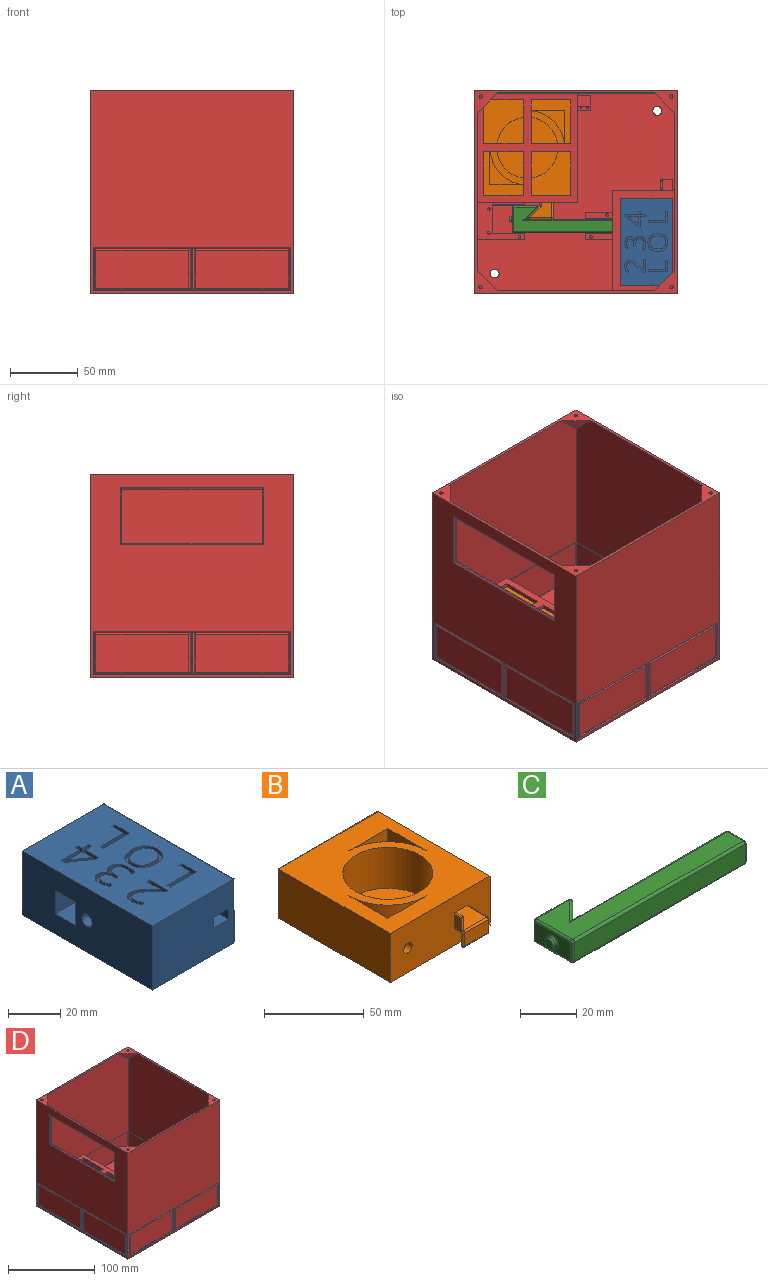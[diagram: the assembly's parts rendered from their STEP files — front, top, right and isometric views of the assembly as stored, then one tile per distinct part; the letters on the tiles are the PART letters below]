
ASSEMBLY  parts=4 mates=2
PART A: 132 faces, bbox 45.2x70.7x31.2 mm
  f0: plane 70.5x44mm, normal (0,0,1), area 2702.5mm2, adj f1,f7,f9,f11,f29,f30,f31,f32
  f1: plane 70.5x30mm, normal (-1,0,0), area 1970.2mm2, adj f0,f7,f9,f10,f18,f24,f25,f26
  f2: plane 8x5mm, normal (0,0,1), area 40mm2, adj f3,f5,f6,f7
  f3: plane 5x5mm, normal (1,0,0), area 25mm2, adj f2,f4,f6,f7
  f4: plane 8x5mm, normal (0,0,-1), area 40mm2, adj f3,f5,f6,f7
  f5: plane 5x5mm, normal (-1,0,0), area 25mm2, adj f2,f4,f6,f7
  f6: plane 8x5mm, normal (0,-1,0), area 40mm2, adj f2,f3,f4,f5
  f7: plane 44x30mm, normal (0,-1,0), area 1280mm2, adj f0,f1,f2,f3,f4,f5,f10,f12
  f8: plane 68.5x28mm, normal (1,0,0), area 1918mm2, adj f11,f12,f13,f14
  f9: plane 44x30mm, normal (0,1,0), area 1280mm2, adj f0,f1,f10,f13,f19,f20,f21,f22
  f10: plane 70.5x44mm, normal (0,0,-1), area 3065.1mm2, adj f1,f7,f9,f14,f15,f130
  f11: cylinder r=1mm len=70.5mm, axis (0,-1,0), area 109.6mm2, adj f0,f8,f12,f13
  f12: cylinder r=1mm len=30mm, axis (0,0,1), area 46mm2, adj f7,f8,f11,f14
  f13: cylinder r=1mm len=30mm, axis (0,0,-1), area 46mm2, adj f8,f9,f11,f14
  f14: cylinder r=1mm len=70.5mm, axis (0,1,0), area 109.6mm2, adj f8,f10,f12,f13
  f15: cylinder r=3.3mm len=17mm, axis (0,0,-1), area 248.2mm2, adj f10,f16,f130,f131
  f16: cone r=0mm half-angle=59deg, axis (0,0,-1), area 39.2mm2, adj f15,f130,f131
  f17: cone r=0mm half-angle=59deg, axis (-1,0,0), area 27.7mm2, adj f18
  f18: cylinder r=2.75mm len=10mm, axis (-1,0,0), area 172.8mm2, adj f1,f17
  f19: plane 5x5mm, normal (1,0,0), area 25mm2, adj f9,f20,f21,f23
  f20: plane 8x5mm, normal (0,0,-1), area 40mm2, adj f9,f19,f22,f23
  f21: plane 8x5mm, normal (0,0,1), area 40mm2, adj f9,f19,f22,f23
  f22: plane 5x5mm, normal (-1,0,0), area 25mm2, adj f9,f20,f21,f23
  f23: plane 8x5mm, normal (0,1,0), area 40mm2, adj f19,f20,f21,f22
  f24: plane 15x11mm, normal (0,0,-1), area 165mm2, adj f1,f25,f27,f28
  f25: plane 15x11mm, normal (0,-1,0), area 165mm2, adj f1,f24,f26,f28
  f26: plane 15x11mm, normal (0,0,1), area 165mm2, adj f1,f25,f27,f28
  f27: plane 15x11mm, normal (0,1,0), area 165mm2, adj f1,f24,f26,f28
  f28: plane 11x11mm, normal (-1,0,0), area 121mm2, adj f24,f25,f26,f27
  f29: plane 9.78x2mm, normal (-1,0,0), area 19.6mm2, adj f0,f30,f48,f49
  f30: plane 2x1.57mm, normal (0,-1,0), area 3.1mm2, adj f0,f29,f31,f49
  f31: plane 7.65x2mm, normal (1,0,0), area 15.3mm2, adj f0,f30,f32,f49
  f32: plane 2x0.08mm, normal (0,-1,0), area 0.2mm2, adj f0,f31,f33,f49
  f33: plane 3.26x3.18mm, normal (-0.71,-0.7,0), area 9.1mm2, adj f0,f32,f34,f49
  f34: extruded ~3.5x2.97mm, area 9.2mm2, adj f0,f33,f35,f49
  f35: extruded ~2.8x2mm, area 5.9mm2, adj f0,f34,f36,f49
  f36: extruded ~2.88x2mm, area 6.4mm2, adj f0,f35,f37,f49
  f37: extruded ~3.29x2mm, area 7.1mm2, adj f0,f36,f38,f49
  f38: extruded ~4.48x2mm, area 9.8mm2, adj f0,f37,f39,f49
  f39: plane 2x1.15mm, normal (-0.61,0.79,0), area 2.9mm2, adj f0,f38,f40,f49
  f40: extruded ~2x1.85mm, area 4.3mm2, adj f0,f39,f41,f49
  f41: extruded ~2x1.75mm, area 3.6mm2, adj f0,f40,f42,f49
  f42: extruded ~2.01x2mm, area 4.4mm2, adj f0,f41,f43,f49
  f43: extruded ~2x1.89mm, area 4.2mm2, adj f0,f42,f44,f49
  f44: extruded ~2x1.58mm, area 3.2mm2, adj f0,f43,f45,f49
  f45: extruded ~2x1.51mm, area 3.5mm2, adj f0,f44,f46,f49
  f46: extruded ~2.59x2.36mm, area 7mm2, adj f0,f45,f47,f49
  f47: plane 3.94x3.92mm, normal (0.71,0.71,0), area 11.1mm2, adj f0,f46,f48,f49
  f48: plane 2x1.46mm, normal (0,1,0), area 2.9mm2, adj f0,f29,f47,f49
  f49: plane 15.08x9.78mm, normal (0,0,1), area 48.7mm2, adj f29,f30,f31,f32,f33,f34,f35,f36
  f50: extruded ~4.39x2mm, area 9.3mm2, adj f51,f65,f66,f128
  f51: extruded ~4.35x2mm, area 9.2mm2, adj f50,f52,f66,f128
  f52: extruded ~3.6x2mm, area 8.1mm2, adj f51,f53,f66,f128
  f53: extruded ~3.56x2mm, area 8mm2, adj f52,f54,f66,f128
  f54: extruded ~4.36x2mm, area 9.2mm2, adj f53,f55,f66,f128
  f55: extruded ~4.4x2mm, area 9.3mm2, adj f54,f56,f66,f128
  f56: extruded ~3.58x2mm, area 8mm2, adj f55,f65,f66,f128
  f57: extruded ~5.38x2mm, area 11.6mm2, adj f0,f58,f64,f66
  f58: extruded ~5.38x2mm, area 11.6mm2, adj f0,f57,f59,f66
  f59: extruded ~4.8x2mm, area 10.7mm2, adj f0,f58,f60,f66
  f60: extruded ~4.87x2mm, area 10.8mm2, adj f0,f59,f61,f66
  f61: extruded ~5.4x2mm, area 11.6mm2, adj f0,f60,f62,f66
  f62: extruded ~5.44x2mm, area 11.7mm2, adj f0,f61,f63,f66
  f63: extruded ~4.86x2mm, area 10.8mm2, adj f0,f62,f64,f66
  f64: extruded ~4.81x2mm, area 10.7mm2, adj f0,f57,f63,f66
  f65: extruded ~3.58x2mm, area 8mm2, adj f50,f56,f66,f128
  f66: plane 14.68x13.11mm, normal (0,0,1), area 64.3mm2, adj f50,f51,f52,f53,f54,f55,f56,f57
  f67: plane 4.94x2mm, normal (0,1,0), area 9.9mm2, adj f68,f83,f84,f129
  f68: plane 5.54x2mm, normal (1,0,0), area 11.1mm2, adj f67,f69,f84,f129
  f69: plane 6.61x4.65mm, normal (-0.58,-0.82,0), area 16.2mm2, adj f68,f70,f84,f129
  f70: extruded ~2x1.62mm, area 3.7mm2, adj f69,f71,f84,f129
  f71: plane 2x0.08mm, normal (-1,0,0), area 0.2mm2, adj f70,f83,f84,f129
  f72: plane 2.21x2mm, normal (-1,0,0), area 4.4mm2, adj f0,f73,f82,f84
  f73: plane 2x1.54mm, normal (0,-1,0), area 3.1mm2, adj f0,f72,f74,f84
  f74: plane 2.21x2mm, normal (1,0,0), area 4.4mm2, adj f0,f73,f75,f84
  f75: plane 10x2mm, normal (0,-1,0), area 20mm2, adj f0,f74,f76,f84
  f76: plane 2x1.79mm, normal (1,0,0), area 3.6mm2, adj f0,f75,f77,f84
  f77: plane 10.06x7.06mm, normal (0.57,0.82,0), area 24.6mm2, adj f0,f76,f78,f84
  f78: plane 2x1.47mm, normal (0,1,0), area 2.9mm2, adj f0,f77,f79,f84
  f79: plane 7.23x2mm, normal (-1,0,0), area 14.5mm2, adj f0,f78,f80,f84
  f80: plane 3.42x2mm, normal (0,1,0), area 6.8mm2, adj f0,f79,f81,f84
  f81: plane 2x1.62mm, normal (-1,0,0), area 3.2mm2, adj f0,f80,f82,f84
  f82: plane 3.42x2mm, normal (0,-1,0), area 6.8mm2, adj f0,f72,f81,f84
  f83: extruded ~3.28x2mm, area 6.6mm2, adj f67,f71,f84,f129
  f84: plane 14.95x11.06mm, normal (0,0,1), area 53.4mm2, adj f67,f68,f69,f70,f71,f72,f73,f74
  f85: plane 14.26x2mm, normal (0,1,0), area 28.5mm2, adj f0,f86,f90,f91
  f86: plane 7.95x2mm, normal (-1,0,0), area 15.9mm2, adj f0,f85,f87,f91
  f87: plane 2x1.5mm, normal (0,-1,0), area 3mm2, adj f0,f86,f88,f91
  f88: plane 6.29x2mm, normal (1,0,0), area 12.6mm2, adj f0,f87,f89,f91
  f89: plane 12.75x2mm, normal (0,-1,0), area 25.5mm2, adj f0,f88,f90,f91
  f90: plane 2x1.66mm, normal (1,0,0), area 3.3mm2, adj f0,f85,f89,f91
  f91: plane 14.26x7.95mm, normal (0,0,1), area 33.1mm2, adj f85,f86,f87,f88,f89,f90
  f92: plane 14.26x2mm, normal (0,1,0), area 28.5mm2, adj f0,f93,f97,f98
  f93: plane 7.95x2mm, normal (-1,0,0), area 15.9mm2, adj f0,f92,f94,f98
  f94: plane 2x1.5mm, normal (0,-1,0), area 3mm2, adj f0,f93,f95,f98
  f95: plane 6.29x2mm, normal (1,0,0), area 12.6mm2, adj f0,f94,f96,f98
  f96: plane 12.75x2mm, normal (0,-1,0), area 25.5mm2, adj f0,f95,f97,f98
  f97: plane 2x1.66mm, normal (1,0,0), area 3.3mm2, adj f0,f92,f96,f98
  f98: plane 14.26x7.95mm, normal (0,0,1), area 33.1mm2, adj f92,f93,f94,f95,f96,f97
  f99: extruded ~2.33x2mm, area 5mm2, adj f0,f100,f126,f127
  f100: extruded ~2.72x2mm, area 6.2mm2, adj f0,f99,f101,f127
  f101: extruded ~3.37x2mm, area 7.2mm2, adj f0,f100,f102,f127
  f102: extruded ~2.52x2mm, area 5.1mm2, adj f0,f101,f103,f127
  f103: extruded ~2.11x2mm, area 4.8mm2, adj f0,f102,f104,f127
  f104: plane 2x1.14mm, normal (-0.6,0.8,0), area 2.8mm2, adj f0,f103,f105,f127
  f105: extruded ~2x1.97mm, area 4.4mm2, adj f0,f104,f106,f127
  f106: extruded ~2x1.84mm, area 3.7mm2, adj f0,f105,f107,f127
  f107: extruded ~2.03x2mm, area 4.3mm2, adj f0,f106,f108,f127
  f108: extruded ~2x1.71mm, area 3.9mm2, adj f0,f107,f109,f127
  f109: extruded ~2.13x2mm, area 4.9mm2, adj f0,f108,f110,f127
  f110: extruded ~2.76x2mm, area 5.8mm2, adj f0,f109,f111,f127
  f111: plane 2x1.48mm, normal (1,0,0), area 3mm2, adj f0,f110,f112,f127
  f112: plane 2x1.45mm, normal (0,1,0), area 2.9mm2, adj f0,f111,f113,f127
  f113: plane 2x1.47mm, normal (-1,0,0), area 2.9mm2, adj f0,f112,f114,f127
  f114: extruded ~4.25x2.71mm, area 11.4mm2, adj f0,f113,f115,f127
  f115: extruded ~3.85x3.02mm, area 11.2mm2, adj f0,f114,f116,f127
  f116: extruded ~2.07x2mm, area 4.2mm2, adj f0,f115,f117,f127
  f117: extruded ~2.06x2mm, area 4.4mm2, adj f0,f116,f118,f127
  f118: plane 2x1.61mm, normal (0,1,0), area 3.2mm2, adj f0,f117,f119,f127
  f119: extruded ~2x1.91mm, area 4mm2, adj f0,f118,f120,f127
  f120: extruded ~2.16x2mm, area 4.3mm2, adj f0,f119,f121,f127
  f121: extruded ~4.19x2mm, area 8.8mm2, adj f0,f120,f122,f127
  f122: extruded ~3.27x2mm, area 7.5mm2, adj f0,f121,f123,f127
  f123: extruded ~2.4x2mm, area 5.2mm2, adj f0,f122,f124,f127
  f124: extruded ~2.65x2mm, area 5.9mm2, adj f0,f123,f125,f127
  f125: plane 2x0.08mm, normal (0,-1,0), area 0.2mm2, adj f0,f124,f126,f127
  f126: extruded ~2.26x2mm, area 5.2mm2, adj f0,f99,f125,f127
  f127: plane 15.29x9.73mm, normal (0,0,1), area 51.4mm2, adj f99,f100,f101,f102,f103,f104,f105,f106
  f128: plane 11.74x9.6mm, normal (0,0,1), area 93.5mm2, adj f50,f51,f52,f53,f54,f55,f56,f65
  f129: plane 8.23x5.65mm, normal (0,0,1), area 22.1mm2, adj f67,f68,f69,f70,f71,f83
  f130: bspline ~18.48x7.59mm, area 185mm2, adj f10,f15,f16,f131
  f131: plane 1.19x1.13mm, normal (0,-0.99,-0.16), area 0.5mm2, adj f15,f16,f130
PART B: 47 faces, bbox 70.5x95x30 mm
  f0: plane 79x70.5mm, normal (0,0,1), area 3654.5mm2, adj f1,f2,f4,f9,f23,f25,f26,f27
  f1: plane 70.5x30mm, normal (0,-1,0), area 1987.6mm2, adj f0,f2,f3,f4,f15,f17,f20,f21
  f2: plane 79x30mm, normal (1,0,0), area 2330mm2, adj f0,f1,f3,f7,f10,f11,f12,f13
  f3: plane 79x70.5mm, normal (0,0,-1), area 5569.5mm2, adj f1,f2,f4,f6
  f4: plane 79x30mm, normal (-1,0,0), area 2370mm2, adj f0,f1,f3,f8
  f5: plane 68.5x28mm, normal (0,1,0), area 1918mm2, adj f6,f7,f8,f9
  f6: cylinder r=1mm len=70.5mm, axis (-1,0,0), area 109.6mm2, adj f3,f5,f7,f8
  f7: cylinder r=1mm len=30mm, axis (0,0,-1), area 46mm2, adj f2,f5,f6,f9
  f8: cylinder r=1mm len=30mm, axis (0,0,1), area 46mm2, adj f4,f5,f6,f9
  f9: cylinder r=1mm len=70.5mm, axis (1,0,0), area 109.6mm2, adj f0,f5,f7,f8
  f10: plane 5x5mm, normal (0,-1,0), area 25mm2, adj f2,f11,f13,f14
  f11: plane 8x5mm, normal (0,0,-1), area 40mm2, adj f2,f10,f12,f14
  f12: plane 5x5mm, normal (0,1,0), area 25mm2, adj f2,f11,f13,f14
  f13: plane 8x5mm, normal (0,0,1), area 40mm2, adj f2,f10,f12,f14
  f14: plane 8x5mm, normal (1,0,0), area 40mm2, adj f10,f11,f12,f13
  f15: cylinder r=3mm len=10mm, axis (0,-1,0), area 188.5mm2, adj f1,f16
  f16: plane 6x6mm, normal (0,-1,0), area 28.3mm2, adj f15
  f17: plane 14x8mm, normal (1,0,0), area 112mm2, adj f1,f40,f43,f46
  f18: plane 16.59x8mm, normal (0,-1,0), area 132.7mm2, adj f36,f41,f42,f46
  f19: plane 8.29x8.29mm, normal (-0.71,0.71,0), area 93.8mm2, adj f20,f35,f36,f37
  f20: plane 8x5mm, normal (-1,0,0), area 40mm2, adj f1,f19,f33,f34
  f21: plane 16.59x14mm, normal (0,0,-1), area 148.9mm2, adj f1,f33,f35,f40,f41
  f22: plane 16.59x14mm, normal (0,0,1), area 148.9mm2, adj f1,f34,f37,f42,f43
  f23: cylinder r=22.5mm len=45mm, axis (0,0,1), area 3534.3mm2, adj f0,f24
  f24: plane 45x45mm, normal (0,0,1), area 1590.4mm2, adj f23
  f25: plane 27.5x25mm, normal (0,-1,0), area 687.5mm2, adj f0,f26,f27,f28
  f26: cylinder r=27.5mm len=27.5mm, axis (0,0,1), area 1079.9mm2, adj f0,f25,f27,f28
  f27: plane 27.5x25mm, normal (-1,0,0), area 687.5mm2, adj f0,f25,f26,f28
  f28: plane 27.5x27.5mm, normal (0,0,1), area 162.3mm2, adj f25,f26,f27
  f29: plane 27.5x25mm, normal (0,1,0), area 687.5mm2, adj f0,f30,f31,f32
  f30: cylinder r=27.5mm len=27.5mm, axis (0,0,1), area 1079.9mm2, adj f0,f29,f31,f32
  f31: plane 27.5x25mm, normal (1,0,0), area 687.5mm2, adj f0,f29,f30,f32
  f32: plane 27.5x27.5mm, normal (0,0,1), area 162.3mm2, adj f29,f30,f31
  f33: cylinder r=1mm len=5.41mm, axis (0,-1,0), area 8.1mm2, adj f1,f20,f21,f35
  f34: cylinder r=1mm len=5.41mm, axis (0,1,0), area 8.1mm2, adj f1,f20,f22,f37
  f35: cylinder r=1mm len=9.29mm, axis (-0.71,-0.71,0), area 18.7mm2, adj f19,f21,f33,f38
  f36: cylinder r=1mm len=8mm, axis (0,0,1), area 18.8mm2, adj f18,f19,f38,f39
  f37: cylinder r=1mm len=9.29mm, axis (0.71,0.71,0), area 18.7mm2, adj f19,f22,f34,f39
  f38: sphere r=1mm, area 2.4mm2, adj f35,f36,f41
  f39: sphere r=1mm, area 2.4mm2, adj f36,f37,f42
  f40: cylinder r=1mm len=14mm, axis (0,1,0), area 22mm2, adj f1,f17,f21,f44
  f41: cylinder r=1mm len=16.59mm, axis (1,0,0), area 26.1mm2, adj f18,f21,f38,f44
  f42: cylinder r=1mm len=16.59mm, axis (-1,0,0), area 26.1mm2, adj f18,f22,f39,f45
  f43: cylinder r=1mm len=14mm, axis (0,-1,0), area 22mm2, adj f1,f17,f22,f45
  f44: sphere r=1mm, area 1.6mm2, adj f40,f41,f46
  f45: sphere r=1mm, area 1.6mm2, adj f42,f43,f46
  f46: cylinder r=1mm len=8mm, axis (0,0,1), area 12.6mm2, adj f17,f18,f44,f45
PART C: 38 faces, bbox 89.8x20x10 mm
  f0: plane 76.75x8mm, normal (0,1,0), area 614mm2, adj f5,f31,f34,f37
  f1: plane 8x8mm, normal (1,0,0), area 64mm2, adj f24,f32,f33,f37
  f2: plane 85.75x8mm, normal (0,-1,0), area 686mm2, adj f14,f23,f24,f25
  f3: plane 18x8mm, normal (-1,0,0), area 115.7mm2, adj f10,f11,f13,f14,f15
  f4: plane 16.59x8mm, normal (0,1,0), area 132.7mm2, adj f11,f17,f20,f21
  f5: plane 8.29x8.29mm, normal (0.71,-0.71,0), area 93.8mm2, adj f0,f21,f27,f30
  f6: plane 85.75x18mm, normal (0,0,-1), area 801.9mm2, adj f13,f17,f23,f27,f31,f32
  f7: plane 85.75x18mm, normal (0,0,1), area 801.9mm2, adj f15,f20,f25,f30,f33,f34
  f8: cylinder r=2mm len=4mm, axis (1,0,0), area 12.6mm2, adj f9,f10
  f9: plane 4x4mm, normal (-1,0,0), area 12.6mm2, adj f8
  f10: torus R=3mm, axis (-1,0,0), area 23.3mm2, adj f3,f8
  f11: cylinder r=1mm len=8mm, axis (0,0,-1), area 12.6mm2, adj f3,f4,f12,f16
  f12: sphere r=1mm, area 1.6mm2, adj f11,f13,f17
  f13: cylinder r=1mm len=18mm, axis (0,-1,0), area 28.3mm2, adj f3,f6,f12,f18
  f14: cylinder r=1mm len=8mm, axis (0,0,1), area 12.6mm2, adj f2,f3,f18,f19
  f15: cylinder r=1mm len=18mm, axis (0,1,0), area 28.3mm2, adj f3,f7,f16,f19
  f16: sphere r=1mm, area 1.6mm2, adj f11,f15,f20
  f17: cylinder r=1mm len=16.59mm, axis (-1,0,0), area 26.1mm2, adj f4,f6,f12,f22
  f18: sphere r=1mm, area 1.6mm2, adj f13,f14,f23
  f19: sphere r=1mm, area 1.6mm2, adj f14,f15,f25
  f20: cylinder r=1mm len=16.59mm, axis (1,0,0), area 26.1mm2, adj f4,f7,f16,f26
  f21: cylinder r=1mm len=8mm, axis (0,0,1), area 18.8mm2, adj f4,f5,f22,f26
  f22: sphere r=1mm, area 2.4mm2, adj f17,f21,f27
  f23: cylinder r=1mm len=85.75mm, axis (1,0,0), area 134.7mm2, adj f2,f6,f18,f28
  f24: cylinder r=1mm len=8mm, axis (0,0,-1), area 12.6mm2, adj f1,f2,f28,f29
  f25: cylinder r=1mm len=85.75mm, axis (-1,0,0), area 134.7mm2, adj f2,f7,f19,f29
  f26: sphere r=1mm, area 2.4mm2, adj f20,f21,f30
  f27: cylinder r=1mm len=10.71mm, axis (0.71,0.71,0), area 19.8mm2, adj f5,f6,f22,f31
  f28: sphere r=1mm, area 1.6mm2, adj f23,f24,f32
  f29: sphere r=1mm, area 1.6mm2, adj f24,f25,f33
  f30: cylinder r=1mm len=10.71mm, axis (-0.71,-0.71,0), area 19.8mm2, adj f5,f7,f26,f34
  f31: cylinder r=1mm len=79.16mm, axis (-1,0,0), area 121.9mm2, adj f0,f6,f27,f35
  f32: cylinder r=1mm len=8mm, axis (0,1,0), area 12.6mm2, adj f1,f6,f28,f35
  f33: cylinder r=1mm len=8mm, axis (0,-1,0), area 12.6mm2, adj f1,f7,f29,f36
  f34: cylinder r=1mm len=79.16mm, axis (1,0,0), area 121.9mm2, adj f0,f7,f30,f36
  f35: sphere r=1mm, area 1.6mm2, adj f31,f32,f37
  f36: sphere r=1mm, area 1.6mm2, adj f33,f34,f37
  f37: cylinder r=1mm len=8mm, axis (0,0,1), area 12.6mm2, adj f0,f1,f35,f36
PART D: 213 faces, bbox 150.1x150.1x150.6 mm
  f0: plane 74.5x34mm, normal (-1,0,0), area 2088mm2, adj f2,f16,f20,f24,f103,f104,f105,f176
  f1: plane 70.5x30mm, normal (1,0,0), area 1994mm2, adj f17,f34,f35,f36,f169,f178,f180,f194
  f2: plane 146x146mm, normal (0,0,1), area 10281.2mm2, adj f0,f4,f5,f6,f8,f13,f19,f20
  f3: plane 64.5x30mm, normal (1,0,0), area 1371.3mm2, adj f5,f14,f15,f77,f171,f172
  f4: plane 148x146mm, normal (1,0,0), area 12523.5mm2, adj f2,f5,f10,f13,f14,f15,f24,f28
  f5: plane 74x34mm, normal (0,-1,0), area 1553.4mm2, adj f2,f3,f4,f6,f10,f15,f163,f164
  f6: plane 80.5x34mm, normal (1,0,0), area 2512.5mm2, adj f2,f5,f9,f10,f13,f153,f154,f155
  f7: plane 79x30mm, normal (-1,0,0), area 2330mm2, adj f11,f130,f132,f133,f155,f156,f157,f158
  f8: plane 17x12.5mm, normal (1,0,0), area 176.5mm2, adj f2,f9,f13,f83,f85,f153,f154,f156
  f9: plane 10x1.5mm, normal (0,0,1), area 10.3mm2, adj f6,f8,f13,f83,f86,f157
  f10: plane 80.5x74mm, normal (0,0,1), area 2216mm2, adj f4,f5,f6,f13,f137,f138,f139,f140
  f11: plane 79x70.5mm, normal (0,0,-1), area 1828.5mm2, adj f7,f131,f132,f134,f137,f138,f139,f140
  f12: plane 150x150mm, normal (0,1,0), area 17892mm2, adj f26,f27,f28,f29,f41,f50,f51,f52
  f13: plane 148x146mm, normal (0,-1,0), area 16734mm2, adj f2,f4,f6,f8,f9,f10,f23,f28
  f14: plane 37x0.5mm, normal (0,0,-1), area 18.5mm2, adj f3,f4,f77,f171
  f15: plane 64.5x0.5mm, normal (0,0,1), area 32.3mm2, adj f3,f4,f5,f77
  f16: plane 74.5x46mm, normal (0,0,1), area 976mm2, adj f0,f20,f23,f24,f126,f127,f128,f129
  f17: plane 70.5x44mm, normal (0,0,-1), area 651mm2, adj f1,f34,f35,f38,f126,f127,f128,f129
  f18: plane 8x1mm, normal (0,0,1), area 8mm2, adj f19,f20,f21,f120
  f19: plane 17x11mm, normal (0,1,0), area 151mm2, adj f2,f18,f21,f22,f23,f116,f117,f119
  f20: plane 46x34mm, normal (0,1,0), area 1358mm2, adj f0,f2,f16,f18,f21,f23,f66,f116
  f21: plane 70.5x30mm, normal (-1,0,0), area 1987mm2, adj f18,f19,f20,f22,f65,f66
  f22: plane 62.5x0.5mm, normal (0,0,-1), area 31.2mm2, adj f19,f21,f23,f65
  f23: plane 148x146mm, normal (-1,0,0), area 16727mm2, adj f2,f13,f16,f19,f20,f22,f24,f28
  f24: plane 148x146mm, normal (0,1,0), area 16939mm2, adj f0,f2,f4,f16,f23,f28,f32,f33
  f25: plane 150x150mm, normal (0,-1,0), area 17860mm2, adj f26,f27,f28,f29,f42,f43,f44,f45
  f26: plane 150x150mm, normal (1,0,0), area 17860mm2, adj f12,f25,f28,f29,f37,f38,f39,f40
  f27: plane 150x150mm, normal (-1,0,0), area 13408mm2, adj f12,f25,f28,f29,f53,f54,f55,f56
  f28: plane 150x150mm, normal (0,0,1), area 1611.1mm2, adj f4,f12,f13,f23,f24,f25,f26,f27
  f29: plane 150x150mm, normal (0,0,-1), area 22361.9mm2, adj f12,f25,f26,f27,f112,f113,f114,f115
  f30: plane 15.14x15.14mm, normal (0.58,-0.58,-0.58), area 188.3mm2, adj f4,f13,f28,f211,f212
  f31: plane 15x15mm, normal (-0.58,-0.58,-0.58), area 188.3mm2, adj f13,f23,f28,f209,f210
  f32: plane 15x15mm, normal (-0.58,0.58,-0.58), area 188.3mm2, adj f23,f24,f28,f207,f208
  f33: plane 15.14x15.14mm, normal (0.58,0.58,-0.58), area 188.3mm2, adj f4,f24,f28,f205,f206
  f34: plane 44x30mm, normal (0,1,0), area 1320mm2, adj f1,f17,f36,f37
  f35: plane 44x30mm, normal (0,-1,0), area 1280mm2, adj f1,f17,f36,f40,f118,f119,f120,f121
  f36: plane 70.5x44mm, normal (0,0,1), area 3065.1mm2, adj f1,f34,f35,f39,f112,f196
  f37: cylinder r=1mm len=32mm, axis (0,0,-1), area 48.3mm2, adj f26,f34,f38,f39
  f38: cylinder r=1mm len=72.5mm, axis (0,1,0), area 111.9mm2, adj f17,f26,f37,f40
  f39: cylinder r=1mm len=72.5mm, axis (0,-1,0), area 111.9mm2, adj f26,f36,f37,f40
  f40: cylinder r=1mm len=32mm, axis (0,0,1), area 48.3mm2, adj f26,f35,f38,f39
  f41: plane 32x1mm, normal (1,0,0), area 30.4mm2, adj f12,f50,f52,f89
  f42: cylinder r=1mm len=32mm, axis (0,0,1), area 48.3mm2, adj f25,f43,f44,f109
  f43: cylinder r=1mm len=72.5mm, axis (1,0,0), area 111.9mm2, adj f25,f42,f45,f111
  f44: cylinder r=1mm len=72.5mm, axis (-1,0,0), area 111.9mm2, adj f25,f42,f45,f108
  f45: cylinder r=1mm len=32mm, axis (0,0,-1), area 48.3mm2, adj f25,f43,f44,f110
  f46: cylinder r=1mm len=72.5mm, axis (1,0,0), area 111.9mm2, adj f25,f47,f48,f101
  f47: cylinder r=1mm len=32mm, axis (0,0,1), area 48.3mm2, adj f25,f46,f49,f99
  f48: cylinder r=1mm len=32mm, axis (0,0,-1), area 48.3mm2, adj f25,f46,f49,f102
  f49: cylinder r=1mm len=72.5mm, axis (-1,0,0), area 111.9mm2, adj f25,f47,f48,f100
  f50: cylinder r=1mm len=71.5mm, axis (1,0,0), area 111.3mm2, adj f12,f41,f51,f91
  f51: cylinder r=1mm len=32mm, axis (0,0,1), area 48.3mm2, adj f12,f50,f52,f92
  f52: cylinder r=1mm len=71.5mm, axis (-1,0,0), area 111.3mm2, adj f12,f41,f51,f90
  f53: cylinder r=1mm len=32mm, axis (0,0,1), area 48.3mm2, adj f27,f54,f55,f80
  f54: cylinder r=1mm len=72.5mm, axis (0,-1,0), area 111.9mm2, adj f27,f53,f56,f82
  f55: cylinder r=1mm len=72.5mm, axis (0,1,0), area 111.9mm2, adj f27,f53,f56,f79
  f56: cylinder r=1mm len=32mm, axis (0,0,-1), area 48.3mm2, adj f27,f54,f55,f81
  f57: cylinder r=1mm len=72.5mm, axis (0,-1,0), area 111.9mm2, adj f27,f58,f59,f75
  f58: cylinder r=1mm len=32mm, axis (0,0,1), area 48.3mm2, adj f27,f57,f60,f73
  f59: cylinder r=1mm len=32mm, axis (0,0,-1), area 48.3mm2, adj f27,f57,f60,f76
  f60: cylinder r=1mm len=72.5mm, axis (0,1,0), area 111.9mm2, adj f27,f58,f59,f74
  f61: cylinder r=1mm len=32mm, axis (0,0,-1), area 48.3mm2, adj f26,f62,f63,f69
  f62: cylinder r=1mm len=72.5mm, axis (0,-1,0), area 111.9mm2, adj f26,f61,f64,f68
  f63: cylinder r=1mm len=72.5mm, axis (0,1,0), area 111.9mm2, adj f26,f61,f64,f71
  f64: cylinder r=1mm len=32mm, axis (0,0,1), area 48.3mm2, adj f26,f62,f63,f70
  f65: plane 30x0.5mm, normal (0,1,0), area 15mm2, adj f21,f22,f23,f66
  f66: plane 70.5x0.5mm, normal (0,0,1), area 35.2mm2, adj f20,f21,f23,f65
  f67: plane 68.5x28mm, normal (1,0,0), area 1918mm2, adj f68,f69,f70,f71
  f68: cylinder r=1mm len=70.5mm, axis (0,-1,0), area 109.6mm2, adj f62,f67,f69,f70
  f69: cylinder r=1mm len=30mm, axis (0,0,-1), area 46mm2, adj f61,f67,f68,f71
  f70: cylinder r=1mm len=30mm, axis (0,0,1), area 46mm2, adj f64,f67,f68,f71
  f71: cylinder r=1mm len=70.5mm, axis (0,1,0), area 109.6mm2, adj f63,f67,f69,f70
  f72: plane 68.5x28mm, normal (-1,0,0), area 1918mm2, adj f73,f74,f75,f76
  f73: cylinder r=1mm len=30mm, axis (0,0,-1), area 46mm2, adj f58,f72,f74,f75
  f74: cylinder r=1mm len=70.5mm, axis (0,-1,0), area 109.6mm2, adj f60,f72,f73,f76
  f75: cylinder r=1mm len=70.5mm, axis (0,1,0), area 109.6mm2, adj f57,f72,f73,f76
  f76: cylinder r=1mm len=30mm, axis (0,0,1), area 46mm2, adj f59,f72,f74,f75
  f77: plane 30x0.5mm, normal (0,-1,0), area 15mm2, adj f3,f4,f14,f15
  f78: plane 68.5x28mm, normal (-1,0,0), area 1918mm2, adj f79,f80,f81,f82
  f79: cylinder r=1mm len=70.5mm, axis (0,-1,0), area 109.6mm2, adj f55,f78,f80,f81
  f80: cylinder r=1mm len=30mm, axis (0,0,-1), area 46mm2, adj f53,f78,f79,f82
  f81: cylinder r=1mm len=30mm, axis (0,0,1), area 46mm2, adj f56,f78,f79,f82
  f82: cylinder r=1mm len=70.5mm, axis (0,1,0), area 109.6mm2, adj f54,f78,f80,f81
  f83: plane 70.5x30mm, normal (0,-1,0), area 1963mm2, adj f8,f9,f84,f85,f86,f87
  f84: plane 30x0.5mm, normal (1,0,0), area 15mm2, adj f13,f83,f85,f87
  f85: plane 61x0.5mm, normal (0,0,-1), area 30.5mm2, adj f8,f13,f83,f84
  f86: plane 14x0.5mm, normal (-1,0,0), area 7mm2, adj f9,f13,f83,f87
  f87: plane 70.5x0.5mm, normal (0,0,1), area 35.3mm2, adj f13,f83,f84,f86
  f88: plane 68.5x28mm, normal (0,1,0), area 1918mm2, adj f89,f90,f91,f92
  f89: cylinder r=1mm len=30mm, axis (0,0,-1), area 46mm2, adj f41,f88,f90,f91
  f90: cylinder r=1mm len=70.5mm, axis (-1,0,0), area 109.6mm2, adj f52,f88,f89,f92
  f91: cylinder r=1mm len=70.5mm, axis (1,0,0), area 109.6mm2, adj f50,f88,f89,f92
  f92: cylinder r=1mm len=30mm, axis (0,0,1), area 46mm2, adj f51,f88,f90,f91
  f93: plane 70.5x30mm, normal (0,1,0), area 2115mm2, adj f94,f95,f96,f97
  f94: plane 30x0.5mm, normal (-1,0,0), area 15mm2, adj f24,f93,f95,f97
  f95: plane 70.5x0.5mm, normal (0,0,-1), area 35.3mm2, adj f24,f93,f94,f96
  f96: plane 30x0.5mm, normal (1,0,0), area 15mm2, adj f24,f93,f95,f97
  f97: plane 70.5x0.5mm, normal (0,0,1), area 35.3mm2, adj f24,f93,f94,f96
  f98: plane 68.5x28mm, normal (0,-1,0), area 1918mm2, adj f99,f100,f101,f102
  f99: cylinder r=1mm len=30mm, axis (0,0,-1), area 46mm2, adj f47,f98,f100,f101
  f100: cylinder r=1mm len=70.5mm, axis (1,0,0), area 109.6mm2, adj f49,f98,f99,f102
  f101: cylinder r=1mm len=70.5mm, axis (-1,0,0), area 109.6mm2, adj f46,f98,f99,f102
  f102: cylinder r=1mm len=30mm, axis (0,0,1), area 46mm2, adj f48,f98,f100,f101
  f103: plane 30x25.5mm, normal (0,1,0), area 765mm2, adj f0,f104,f105,f106
  f104: plane 25.5x0.5mm, normal (0,0,-1), area 12.7mm2, adj f0,f24,f103,f106
  f105: plane 25.5x0.5mm, normal (0,0,1), area 12.7mm2, adj f0,f24,f103,f106
  f106: plane 30x0.5mm, normal (-1,0,0), area 15mm2, adj f24,f103,f104,f105
  f107: plane 68.5x28mm, normal (0,-1,0), area 1918mm2, adj f108,f109,f110,f111
  f108: cylinder r=1mm len=70.5mm, axis (1,0,0), area 109.6mm2, adj f44,f107,f109,f110
  f109: cylinder r=1mm len=30mm, axis (0,0,-1), area 46mm2, adj f42,f107,f108,f111
  f110: cylinder r=1mm len=30mm, axis (0,0,1), area 46mm2, adj f45,f107,f108,f111
  f111: cylinder r=1mm len=70.5mm, axis (-1,0,0), area 109.6mm2, adj f43,f107,f109,f110
  f112: cylinder r=3.3mm len=6.6mm, axis (0,0,-1), area 44.1mm2, adj f29,f36,f195,f196
  f113: cylinder r=3.3mm len=6.6mm, axis (0,0,-1), area 41.5mm2, adj f2,f29
  f114: cylinder r=3.3mm len=6.6mm, axis (0,0,-1), area 62.2mm2, adj f29,f130
  f115: cylinder r=3.3mm len=6.6mm, axis (0,0,-1), area 41.5mm2, adj f2,f29
  f116: plane 8x1.5mm, normal (0,0,1), area 10.5mm2, adj f19,f20,f117,f119,f123,f124
  f117: plane 17x8mm, normal (-1,0,0), area 136mm2, adj f2,f19,f20,f116
  f118: plane 8x3mm, normal (0,0,-1), area 24mm2, adj f20,f35,f119,f120
  f119: plane 11x5mm, normal (1,0,0), area 43mm2, adj f19,f20,f35,f116,f118,f121
  f120: plane 11x5mm, normal (-1,0,0), area 43mm2, adj f18,f19,f20,f35,f118,f121
  f121: plane 11x8mm, normal (0,0,1), area 88mm2, adj f19,f35,f119,f120
  f122: plane 0.99x0.99mm, normal (0,0,1), area 0.8mm2, adj f123
  f123: cylinder r=0.49mm len=1mm, axis (0,0,1), area 3.1mm2, adj f116,f122
  f124: cylinder r=0.48mm len=1mm, axis (0,0,1), area 3mm2, adj f116,f125
  f125: plane 0.97x0.97mm, normal (0,0,1), area 0.7mm2, adj f124
  f126: plane 38x3mm, normal (0,1,0), area 114mm2, adj f16,f17,f127,f129
  f127: plane 64.5x3mm, normal (-1,0,0), area 193.5mm2, adj f16,f17,f126,f128
  f128: plane 38x3mm, normal (0,-1,0), area 114mm2, adj f16,f17,f127,f129
  f129: plane 64.5x3mm, normal (1,0,0), area 193.5mm2, adj f16,f17,f126,f128
  f130: plane 79x70.5mm, normal (0,0,1), area 5535.3mm2, adj f7,f114,f131,f132,f135
  f131: plane 79x30mm, normal (1,0,0), area 2370mm2, adj f11,f130,f132,f136
  f132: plane 70.5x30mm, normal (0,1,0), area 1915mm2, adj f7,f11,f130,f131,f163,f164,f165,f166
  f133: cylinder r=1mm len=32mm, axis (0,0,-1), area 48.3mm2, adj f7,f12,f134,f135
  f134: cylinder r=1mm len=72.5mm, axis (1,0,0), area 111.9mm2, adj f11,f12,f133,f136
  f135: cylinder r=1mm len=72.5mm, axis (-1,0,0), area 111.9mm2, adj f12,f130,f133,f136
  f136: cylinder r=1mm len=32mm, axis (0,0,1), area 48.3mm2, adj f12,f131,f134,f135
  f137: plane 29x3mm, normal (0,-1,0), area 87mm2, adj f10,f11,f138,f140
  f138: plane 32.25x3mm, normal (1,0,0), area 96.7mm2, adj f10,f11,f137,f139
  f139: plane 29x3mm, normal (0,1,0), area 87mm2, adj f10,f11,f138,f140
  f140: plane 32.25x3mm, normal (-1,0,0), area 96.7mm2, adj f10,f11,f137,f139
  f141: plane 32.25x3mm, normal (1,0,0), area 96.7mm2, adj f10,f11,f142,f144
  f142: plane 29x3mm, normal (0,1,0), area 87mm2, adj f10,f11,f141,f143
  f143: plane 32.25x3mm, normal (-1,0,0), area 96.7mm2, adj f10,f11,f142,f144
  f144: plane 29x3mm, normal (0,-1,0), area 87mm2, adj f10,f11,f141,f143
  f145: plane 29x3mm, normal (0,1,0), area 87mm2, adj f10,f11,f146,f148
  f146: plane 32.25x3mm, normal (-1,0,0), area 96.7mm2, adj f10,f11,f145,f147
  f147: plane 29x3mm, normal (0,-1,0), area 87mm2, adj f10,f11,f146,f148
  f148: plane 32.25x3mm, normal (1,0,0), area 96.7mm2, adj f10,f11,f145,f147
  f149: plane 29x3mm, normal (0,-1,0), area 87mm2, adj f10,f11,f150,f152
  f150: plane 32.25x3mm, normal (1,0,0), area 96.7mm2, adj f10,f11,f149,f151
  f151: plane 29x3mm, normal (0,1,0), area 87mm2, adj f10,f11,f150,f152
  f152: plane 32.25x3mm, normal (-1,0,0), area 96.7mm2, adj f10,f11,f149,f151
  f153: plane 10x3mm, normal (0,0,1), area 28.4mm2, adj f6,f8,f154,f158,f160,f161
  f154: plane 17x10mm, normal (0,-1,0), area 170mm2, adj f2,f6,f8,f153
  f155: plane 8x2.5mm, normal (0,0,-1), area 20mm2, adj f6,f7,f157,f158
  f156: plane 12.5x8mm, normal (0,0,1), area 100mm2, adj f7,f8,f157,f158
  f157: plane 12.5x5mm, normal (0,-1,0), area 47.5mm2, adj f6,f7,f8,f9,f155,f156
  f158: plane 12.5x5mm, normal (0,1,0), area 47.5mm2, adj f6,f7,f8,f153,f155,f156
  f159: plane 1x1mm, normal (0,0,1), area 0.8mm2, adj f160
  f160: cylinder r=0.5mm len=1mm, axis (0,0,1), area 3.1mm2, adj f153,f159
  f161: cylinder r=0.5mm len=1mm, axis (0,0,1), area 3.1mm2, adj f153,f162
  f162: plane 1x1mm, normal (0,0,1), area 0.8mm2, adj f161
  f163: plane 20x2.5mm, normal (0,0,-1), area 50mm2, adj f5,f132,f164,f166
  f164: plane 10x2.5mm, normal (1,0,0), area 25mm2, adj f5,f132,f163,f165
  f165: plane 20x2.5mm, normal (0,0,1), area 50mm2, adj f5,f132,f164,f166
  f166: plane 10x2.5mm, normal (-1,0,0), area 25mm2, adj f5,f132,f163,f165
  f167: plane 24x21mm, normal (0,0,1), area 504mm2, adj f168,f173,f174,f175
  f168: plane 27.5x21.5mm, normal (1,0,0), area 360.3mm2, adj f2,f5,f167,f171,f172,f173,f175
  f169: plane 23x11mm, normal (0,0,1), area 253mm2, adj f1,f170,f178,f180
  f170: plane 21.5x20mm, normal (-1,0,0), area 309mm2, adj f2,f169,f176,f177,f178,f179,f180,f181
  f171: plane 35.25x21.5mm, normal (0,-1,0), area 747.6mm2, adj f2,f3,f4,f14,f168,f172
  f172: plane 34.75x27.5mm, normal (0,0,1), area 442.2mm2, adj f3,f5,f168,f171,f173,f174,f175,f182
  f173: plane 24x11mm, normal (0,-1,0), area 264mm2, adj f167,f168,f172,f174
  f174: plane 21x11mm, normal (1,0,0), area 206.4mm2, adj f167,f172,f173,f175,f193
  f175: plane 24x11mm, normal (0,1,0), area 264mm2, adj f167,f168,f172,f174
  f176: plane 20x4.5mm, normal (0,0,1), area 86.9mm2, adj f0,f170,f177,f178,f188
  f177: plane 21.5x20mm, normal (0,1,0), area 430mm2, adj f0,f2,f170,f176
  f178: plane 23x11mm, normal (0,-1,0), area 253mm2, adj f1,f169,f170,f176,f194
  f179: plane 20x4.5mm, normal (0,0,1), area 86.9mm2, adj f0,f170,f180,f181,f190
  f180: plane 23x11mm, normal (0,1,0), area 253mm2, adj f1,f169,f170,f179,f194
  f181: plane 21.5x20mm, normal (0,-1,0), area 430mm2, adj f0,f2,f170,f179
  f182: cylinder r=1mm len=2mm, axis (0,0,-1), area 6.3mm2, adj f172,f183
  f183: plane 2x2mm, normal (0,0,1), area 3.1mm2, adj f182
  f184: cylinder r=1mm len=2mm, axis (0,0,-1), area 6.3mm2, adj f172,f185
  f185: plane 2x2mm, normal (0,0,1), area 3.1mm2, adj f184
  f186: cylinder r=1mm len=2mm, axis (0,0,-1), area 6.3mm2, adj f172,f187
  f187: plane 2x2mm, normal (0,0,1), area 3.1mm2, adj f186
  f188: cylinder r=1mm len=2mm, axis (0,0,-1), area 6.3mm2, adj f176,f189
  f189: plane 2x2mm, normal (0,0,1), area 3.1mm2, adj f188
  f190: cylinder r=1mm len=2mm, axis (0,0,-1), area 6.3mm2, adj f179,f191
  f191: plane 2x2mm, normal (0,0,1), area 3.1mm2, adj f190
  f192: plane 5.6x5.6mm, normal (1,0,0), area 24.6mm2, adj f193
  f193: cylinder r=2.8mm len=7.75mm, axis (1,0,0), area 136.3mm2, adj f174,f192
  f194: plane 11x3mm, normal (0,0,-1), area 33mm2, adj f0,f1,f178,f180
  f195: plane 0.64x0.64mm, normal (0,0.99,0.16), area 0.2mm2, adj f29,f112,f196
  f196: bspline ~7.59x7.59mm, area 30.8mm2, adj f29,f36,f112,f195
  f197: plane 40x1mm, normal (0,-1,0), area 40mm2, adj f4,f198,f199,f202
  f198: plane 104x1mm, normal (0,0,-1), area 104mm2, adj f4,f197,f200,f201
  f199: plane 104x1mm, normal (0,0,1), area 104mm2, adj f4,f197,f200,f204
  f200: plane 40x1mm, normal (0,1,0), area 40mm2, adj f4,f198,f199,f203
  f201: cylinder r=1mm len=106mm, axis (0,-1,0), area 164.5mm2, adj f27,f198,f202,f203
  f202: cylinder r=1mm len=42mm, axis (0,0,1), area 64mm2, adj f27,f197,f201,f204
  f203: cylinder r=1mm len=42mm, axis (0,0,-1), area 64mm2, adj f27,f200,f201,f204
  f204: cylinder r=1mm len=106mm, axis (0,1,0), area 164.5mm2, adj f27,f199,f202,f203
  f205: cylinder r=1.35mm len=10mm, axis (0,0,1), area 77.4mm2, adj f28,f33,f206
  f206: plane 2.02x2.02mm, normal (0,0,1), area 1.9mm2, adj f33,f205
  f207: cylinder r=1.35mm len=10mm, axis (0,0,1), area 77.4mm2, adj f28,f32,f208
  f208: plane 2.02x2.02mm, normal (0,0,1), area 1.9mm2, adj f32,f207
  f209: cylinder r=1.35mm len=10mm, axis (0,0,1), area 77.4mm2, adj f28,f31,f210
  f210: plane 2.02x2.02mm, normal (0,0,1), area 1.9mm2, adj f31,f209
  f211: cylinder r=1.35mm len=10mm, axis (0,0,1), area 77.4mm2, adj f28,f30,f212
  f212: plane 2.02x2.02mm, normal (0,0,1), area 1.9mm2, adj f30,f211
PLACE A at identity
PLACE B at identity
PLACE C at identity
PLACE D at identity fixed
MATE slider B.f1 <-> D.f132  axis (0,1,0) through (-1.5,-5,33)mm
MATE slider C.f8 <-> D.f193  axis (-1,0,0) through (-46.75,-20,18)mm
